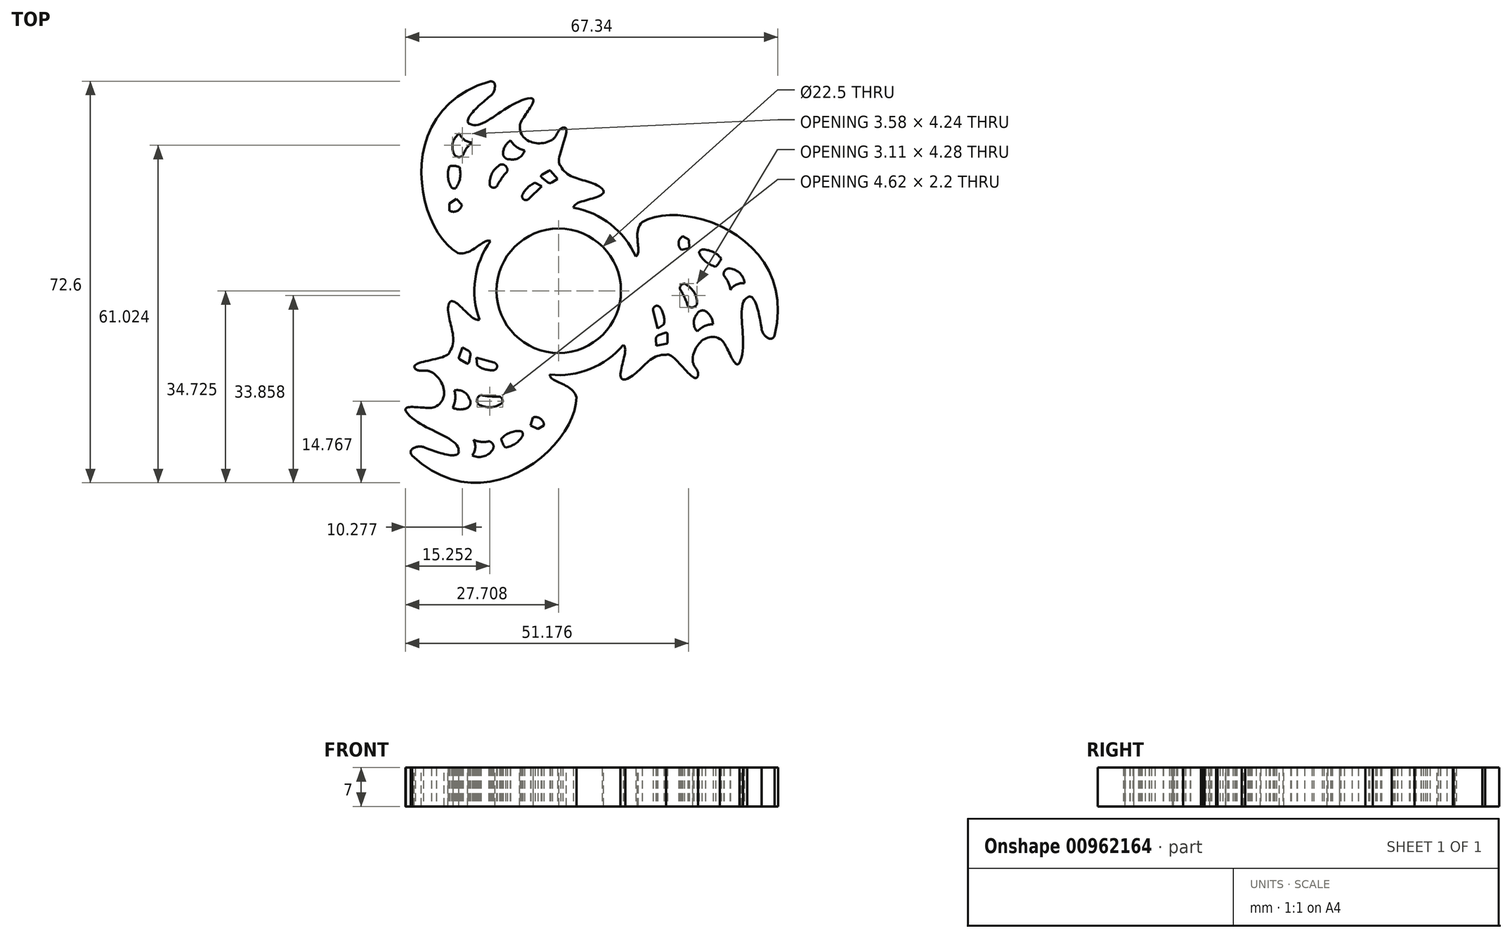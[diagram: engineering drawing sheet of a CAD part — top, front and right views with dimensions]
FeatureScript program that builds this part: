
annotation { "Feature Type Name" : "Feature", "Feature Type Description" : "" }
export const myFeature = defineFeature(function(context is Context, id is Id, definition is map)
    precondition{}
    {
        {
            var Q0;
            Q0=qCreatedBy(makeId("Top.planeOp"),FACE);
            var sketch = newSketch(context, id + "F0", { "sketchPlane" : qUnion([Q0])});
            skCircle(sketch, "E0", {"center": v(0.74, -90.82) * mm, "radius": 11.25 * mm});
            skCircle(sketch, "E1.0", {"center": v(0.74, -90.82) * mm, "radius": 15.25 * mm});
            skFitSpline(sketch, "E2", {"points": [v(-11.6, -81.84) * mm, v(-17.53, -83.96) * mm], "startDerivative": vector(-4, 2.16) * mm, "endDerivative": vector(-7.86, 2) * mm});
            skFitSpline(sketch, "E3", {"points": [v(-17.53, -83.96) * mm, v(-11.8, -52.97) * mm], "startDerivative": vector(-23.07, 13.08) * mm, "endDerivative": vector(52.2, 15.17) * mm});
            skFitSpline(sketch, "E4", {"points": [v(-11.8, -52.97) * mm, v(-11.47, -55.48) * mm], "startDerivative": vector(4.5, 0.84) * mm, "endDerivative": vector(-2.3, -1.99) * mm});
            skFitSpline(sketch, "E5", {"points": [v(-11.47, -55.48) * mm, v(-15.25, -60.7) * mm], "startDerivative": vector(-5.39, -4.17) * mm, "endDerivative": vector(5.26, -2.02) * mm});
            skFitSpline(sketch, "E6", {"points": [v(-15.25, -60.7) * mm, v(-4.3, -55.98) * mm], "startDerivative": vector(7.24, -3.74) * mm, "endDerivative": vector(12.54, 1.2) * mm});
            skFitSpline(sketch, "E7", {"points": [v(-4.3, -55.98) * mm, v(-6.3, -61.23) * mm], "startDerivative": vector(5.26, -0.77) * mm, "endDerivative": vector(0.49, -4.52) * mm});
            skFitSpline(sketch, "E8", {"points": [v(-6.3, -61.23) * mm, v(-0.45, -63.53) * mm], "startDerivative": vector(0.14, -8.53) * mm, "endDerivative": vector(6.56, 4) * mm});
            skFitSpline(sketch, "E9", {"points": [v(-0.45, -63.53) * mm, v(1.48, -61.32) * mm], "startDerivative": vector(2.9, 1.83) * mm, "endDerivative": vector(3, 0.9) * mm});
            skFitSpline(sketch, "E10", {"points": [v(1.48, -61.32) * mm, v(1.08, -68.23) * mm], "startDerivative": vector(6.34, 1.41) * mm, "endDerivative": vector(4.15, -2.92) * mm});
            skFitSpline(sketch, "E11", {"points": [v(1.08, -68.23) * mm, v(8.6, -72.36) * mm], "startDerivative": vector(4.35, -8.75) * mm, "endDerivative": vector(6.74, -5.79) * mm});
            skFitSpline(sketch, "E12", {"points": [v(8.6, -72.36) * mm, v(3.4, -75.8) * mm], "startDerivative": vector(4.7, -5.65) * mm, "endDerivative": vector(-0.3, -4.9) * mm});
            skArc(sketch, "E13", {"start": v(-17.21, -62.4) * mm, "mid": v(-16.3, -63.55) * mm, "end": v(-14.9, -64.02) * mm});
            skArc(sketch, "E14", {"start": v(-17.21, -62.4) * mm, "mid": v(-18.38, -64) * mm, "end": v(-18.23, -65.98) * mm});
            skArc(sketch, "E15", {"start": v(-18.23, -65.98) * mm, "mid": v(-17.47, -66.62) * mm, "end": v(-16.53, -66.27) * mm});
            skArc(sketch, "E16", {"start": v(-14.9, -64.02) * mm, "mid": v(-15.9, -65.01) * mm, "end": v(-16.53, -66.27) * mm});
            skArc(sketch, "E17", {"start": v(-17.9, -72.28) * mm, "mid": v(-17.1, -70.45) * mm, "end": v(-17.21, -68.45) * mm});
            skArc(sketch, "E18", {"start": v(-19, -68.3) * mm, "mid": v(-19.28, -70.25) * mm, "end": v(-18.65, -72.11) * mm});
            skArc(sketch, "E19", {"start": v(-18.65, -72.11) * mm, "mid": v(-18.3, -72.31) * mm, "end": v(-17.9, -72.28) * mm});
            skArc(sketch, "E20", {"start": v(-17.21, -68.45) * mm, "mid": v(-18.1, -68.24) * mm, "end": v(-19, -68.3) * mm});
            skArc(sketch, "E21", {"start": v(-9.73, -67.97) * mm, "mid": v(-11.32, -69.58) * mm, "end": v(-11.7, -71.8) * mm});
            skArc(sketch, "E22", {"start": v(-11.7, -71.8) * mm, "mid": v(-11.13, -72.18) * mm, "end": v(-10.48, -71.97) * mm});
            skArc(sketch, "E23", {"start": v(-8.56, -69.2) * mm, "mid": v(-9.6, -70.53) * mm, "end": v(-10.48, -71.97) * mm});
            skArc(sketch, "E24", {"start": v(-8.56, -69.2) * mm, "mid": v(-8.83, -68.29) * mm, "end": v(-9.73, -67.97) * mm});
            skArc(sketch, "E25", {"start": v(-7.98, -63.64) * mm, "mid": v(-8.94, -64.65) * mm, "end": v(-9.35, -65.98) * mm});
            skArc(sketch, "E26", {"start": v(-9.35, -65.98) * mm, "mid": v(-8.94, -66.8) * mm, "end": v(-8.05, -67.05) * mm});
            skArc(sketch, "E27", {"start": v(-8.05, -67.05) * mm, "mid": v(-6.43, -66.76) * mm, "end": v(-5.43, -65.46) * mm});
            skArc(sketch, "E28", {"start": v(-7.98, -63.64) * mm, "mid": v(-6.88, -64.8) * mm, "end": v(-5.43, -65.46) * mm});
            skArc(sketch, "E29", {"start": v(-19, -76.35) * mm, "mid": v(-17.63, -76.39) * mm, "end": v(-16.77, -75.31) * mm});
            skLineSegment(sketch, "E30", {"start": v(-19, -76.35) * mm, "end": v(-19, -75.05) * mm});
            skLineSegment(sketch, "E31", {"start": v(-19, -75.05) * mm, "end": v(-17.77, -74.22) * mm});
            skLineSegment(sketch, "E32", {"start": v(-17.77, -74.22) * mm, "end": v(-16.77, -75.31) * mm});
            skLineSegment(sketch, "E33", {"start": v(-3.53, -71.3) * mm, "end": v(-2.3, -71.91) * mm});
            skLineSegment(sketch, "E34", {"start": v(-2.3, -71.91) * mm, "end": v(-4.7, -74.23) * mm});
            skArc(sketch, "E35", {"start": v(-5.8, -73.43) * mm, "mid": v(-5.6, -74.3) * mm, "end": v(-4.7, -74.23) * mm});
            skArc(sketch, "E36", {"start": v(-3.53, -71.3) * mm, "mid": v(-4.87, -72.15) * mm, "end": v(-5.8, -73.43) * mm});
            skArc(sketch, "E37", {"start": v(-2.3, -69.83) * mm, "mid": v(-2.44, -70.06) * mm, "end": v(-2.34, -70.32) * mm});
            skLineSegment(sketch, "E38", {"start": v(-2.3, -69.83) * mm, "end": v(-1.05, -69.13) * mm});
            skArc(sketch, "E39", {"start": v(-0.73, -69.13) * mm, "mid": v(-0.9, -69.09) * mm, "end": v(-1.05, -69.13) * mm});
            skLineSegment(sketch, "E40", {"start": v(-0.73, -69.13) * mm, "end": v(0.54, -70.6) * mm});
            skLineSegment(sketch, "E41", {"start": v(0.54, -70.6) * mm, "end": v(-0.47, -71.23) * mm});
            skArc(sketch, "E42", {"start": v(-1.3, -71.18) * mm, "mid": v(-0.9, -71.34) * mm, "end": v(-0.47, -71.23) * mm});
            skLineSegment(sketch, "E43", {"start": v(-1.3, -71.18) * mm, "end": v(-2.34, -70.32) * mm});
            skLineSegment(sketch, "E44", {"start": v(-11.6, -81.84) * mm, "end": v(-10.71, -82.21) * mm});
            skLineSegment(sketch, "E45", {"start": v(3.4, -75.8) * mm, "end": v(3.39, -75.8) * mm});
            skArc(sketch, "E46.1.0", {"start": v(-13.81, -111.3) * mm, "mid": v(-11.62, -111.87) * mm, "end": v(-9.5, -111.1) * mm});
            skArc(sketch, "E46.1.1", {"start": v(-14.64, -117.76) * mm, "mid": v(-13.29, -118.13) * mm, "end": v(-11.89, -118.04) * mm});
            skArc(sketch, "E46.1.2", {"start": v(-9.65, -117.54) * mm, "mid": v(-9.4, -118.42) * mm, "end": v(-8.88, -119.17) * mm});
            skArc(sketch, "E46.1.3", {"start": v(-14.9, -120.57) * mm, "mid": v(-12.92, -120.78) * mm, "end": v(-11.29, -119.67) * mm});
            skArc(sketch, "E46.1.4", {"start": v(-6, -116.22) * mm, "mid": v(-7.98, -116.44) * mm, "end": v(-9.65, -117.54) * mm});
            skArc(sketch, "E46.1.5", {"start": v(-1.92, -115.15) * mm, "mid": v(-2.57, -113.94) * mm, "end": v(-3.93, -113.73) * mm});
            skArc(sketch, "E46.1.6", {"start": v(-13.33, -109.67) * mm, "mid": v(-11.66, -109.91) * mm, "end": v(-9.97, -109.96) * mm});
            skArc(sketch, "E46.1.7", {"start": v(-18.44, -111.95) * mm, "mid": v(-17.09, -112.28) * mm, "end": v(-15.73, -111.97) * mm});
            skArc(sketch, "E46.1.8", {"start": v(-18.44, -111.95) * mm, "mid": v(-17.98, -110.42) * mm, "end": v(-18.14, -108.83) * mm});
            skArc(sketch, "E46.1.9", {"start": v(-15.73, -111.97) * mm, "mid": v(-15.22, -111.2) * mm, "end": v(-15.45, -110.3) * mm});
            skArc(sketch, "E46.1.10", {"start": v(-15.45, -110.3) * mm, "mid": v(-16.5, -109.05) * mm, "end": v(-18.14, -108.83) * mm});
            skArc(sketch, "E46.1.11", {"start": v(-14.9, -120.57) * mm, "mid": v(-14.36, -119.2) * mm, "end": v(-14.64, -117.76) * mm});
            skArc(sketch, "E46.1.12", {"start": v(-13.33, -109.67) * mm, "mid": v(-13.99, -110.37) * mm, "end": v(-13.81, -111.3) * mm});
            skArc(sketch, "E46.1.13", {"start": v(-11.29, -119.67) * mm, "mid": v(-11.1, -118.68) * mm, "end": v(-11.89, -118.04) * mm});
            skArc(sketch, "E46.1.14", {"start": v(-9.5, -111.1) * mm, "mid": v(-9.47, -110.42) * mm, "end": v(-9.97, -109.96) * mm});
            skArc(sketch, "E46.1.15", {"start": v(-5.76, -116.96) * mm, "mid": v(-5.77, -116.56) * mm, "end": v(-6, -116.22) * mm});
            skArc(sketch, "E46.1.16", {"start": v(-8.88, -119.17) * mm, "mid": v(-7.06, -118.43) * mm, "end": v(-5.76, -116.96) * mm});
            skLineSegment(sketch, "E46.1.17", {"start": v(-4.38, -115.14) * mm, "end": v(-3.93, -113.73) * mm});
            skLineSegment(sketch, "E46.1.18", {"start": v(-14.11, -102.9) * mm, "end": v(-10.9, -103.82) * mm});
            skLineSegment(sketch, "E46.1.19", {"start": v(-1.92, -115.15) * mm, "end": v(-3.04, -115.8) * mm});
            skLineSegment(sketch, "E46.1.20", {"start": v(-0.87, -105.98) * mm, "end": v(-0.99, -105.03) * mm});
            skArc(sketch, "E46.1.21", {"start": v(-14.03, -104.27) * mm, "mid": v(-12.62, -105) * mm, "end": v(-11.05, -105.18) * mm});
            skArc(sketch, "E46.1.22", {"start": v(-11.05, -105.18) * mm, "mid": v(-10.4, -104.56) * mm, "end": v(-10.9, -103.82) * mm});
            skLineSegment(sketch, "E46.1.23", {"start": v(-3.04, -115.8) * mm, "end": v(-4.38, -115.14) * mm});
            skLineSegment(sketch, "E46.1.24", {"start": v(-17.3, -102.93) * mm, "end": v(-16.67, -101.1) * mm});
            skLineSegment(sketch, "E46.1.25", {"start": v(-13.6, -96.02) * mm, "end": v(-13.59, -96.02) * mm});
            skArc(sketch, "E46.1.26", {"start": v(-17.3, -102.93) * mm, "mid": v(-17.26, -103.1) * mm, "end": v(-17.15, -103.2) * mm});
            skArc(sketch, "E46.1.27", {"start": v(-15.25, -102.4) * mm, "mid": v(-15.31, -101.97) * mm, "end": v(-15.62, -101.66) * mm});
            skArc(sketch, "E46.1.28", {"start": v(-15.92, -103.93) * mm, "mid": v(-15.64, -103.94) * mm, "end": v(-15.48, -103.73) * mm});
            skLineSegment(sketch, "E46.1.29", {"start": v(-14.03, -104.27) * mm, "end": v(-14.11, -102.9) * mm});
            skLineSegment(sketch, "E46.1.30", {"start": v(-15.25, -102.4) * mm, "end": v(-15.48, -103.73) * mm});
            skLineSegment(sketch, "E46.1.31", {"start": v(-15.92, -103.93) * mm, "end": v(-17.15, -103.2) * mm});
            skLineSegment(sketch, "E46.1.32", {"start": v(-16.67, -101.1) * mm, "end": v(-15.62, -101.66) * mm});
            skArc(sketch, "E46.2.0", {"start": v(25.76, -93.17) * mm, "mid": v(25.16, -91) * mm, "end": v(23.42, -89.54) * mm});
            skArc(sketch, "E46.2.1", {"start": v(31.76, -90.67) * mm, "mid": v(31.4, -89.3) * mm, "end": v(30.63, -88.14) * mm});
            skArc(sketch, "E46.2.2", {"start": v(29.08, -86.45) * mm, "mid": v(29.7, -85.79) * mm, "end": v(30.1, -84.97) * mm});
            skArc(sketch, "E46.2.3", {"start": v(34.33, -89.48) * mm, "mid": v(33.52, -87.67) * mm, "end": v(31.74, -86.8) * mm});
            skArc(sketch, "E46.2.4", {"start": v(26.1, -83.94) * mm, "mid": v(27.3, -85.55) * mm, "end": v(29.08, -86.45) * mm});
            skArc(sketch, "E46.2.5", {"start": v(23.14, -80.95) * mm, "mid": v(22.42, -82.12) * mm, "end": v(22.92, -83.4) * mm});
            skArc(sketch, "E46.2.6", {"start": v(24.1, -93.57) * mm, "mid": v(23.48, -92) * mm, "end": v(22.67, -90.52) * mm});
            skArc(sketch, "E46.2.7", {"start": v(28.63, -96.85) * mm, "mid": v(28.24, -95.52) * mm, "end": v(27.3, -94.5) * mm});
            skArc(sketch, "E46.2.8", {"start": v(28.63, -96.85) * mm, "mid": v(27.08, -97.22) * mm, "end": v(25.78, -98.16) * mm});
            skArc(sketch, "E46.2.9", {"start": v(27.3, -94.5) * mm, "mid": v(26.37, -94.44) * mm, "end": v(25.71, -95.09) * mm});
            skArc(sketch, "E46.2.10", {"start": v(25.71, -95.09) * mm, "mid": v(25.15, -96.63) * mm, "end": v(25.78, -98.16) * mm});
            skArc(sketch, "E46.2.11", {"start": v(34.33, -89.48) * mm, "mid": v(32.87, -89.7) * mm, "end": v(31.76, -90.67) * mm});
            skArc(sketch, "E46.2.12", {"start": v(24.1, -93.57) * mm, "mid": v(25.03, -93.8) * mm, "end": v(25.76, -93.17) * mm});
            skArc(sketch, "E46.2.13", {"start": v(31.74, -86.8) * mm, "mid": v(30.8, -87.14) * mm, "end": v(30.63, -88.14) * mm});
            skArc(sketch, "E46.2.14", {"start": v(23.42, -89.54) * mm, "mid": v(22.82, -89.85) * mm, "end": v(22.67, -90.52) * mm});
            skArc(sketch, "E46.2.15", {"start": v(26.63, -83.37) * mm, "mid": v(26.28, -83.58) * mm, "end": v(26.1, -83.94) * mm});
            skArc(sketch, "E46.2.16", {"start": v(30.1, -84.97) * mm, "mid": v(28.55, -83.76) * mm, "end": v(26.63, -83.37) * mm});
            skLineSegment(sketch, "E46.2.17", {"start": v(24.36, -83.08) * mm, "end": v(22.92, -83.4) * mm});
            skLineSegment(sketch, "E46.2.18", {"start": v(18.63, -97.63) * mm, "end": v(17.82, -94.4) * mm});
            skLineSegment(sketch, "E46.2.19", {"start": v(23.14, -80.95) * mm, "end": v(24.26, -81.6) * mm});
            skLineSegment(sketch, "E46.2.20", {"start": v(14.68, -84.62) * mm, "end": v(13.91, -85.2) * mm});
            skArc(sketch, "E46.2.21", {"start": v(19.78, -96.88) * mm, "mid": v(19.7, -95.3) * mm, "end": v(19.07, -93.84) * mm});
            skArc(sketch, "E46.2.22", {"start": v(19.07, -93.84) * mm, "mid": v(18.21, -93.6) * mm, "end": v(17.82, -94.4) * mm});
            skLineSegment(sketch, "E46.2.23", {"start": v(24.26, -81.6) * mm, "end": v(24.36, -83.08) * mm});
            skLineSegment(sketch, "E46.2.24", {"start": v(20.26, -100.39) * mm, "end": v(18.35, -100.75) * mm});
            skLineSegment(sketch, "E46.2.25", {"start": v(12.42, -100.62) * mm, "end": v(12.41, -100.62) * mm});
            skArc(sketch, "E46.2.26", {"start": v(20.26, -100.39) * mm, "mid": v(20.37, -100.27) * mm, "end": v(20.42, -100.1) * mm});
            skArc(sketch, "E46.2.27", {"start": v(18.77, -98.87) * mm, "mid": v(18.42, -99.14) * mm, "end": v(18.3, -99.56) * mm});
            skArc(sketch, "E46.2.28", {"start": v(20.43, -98.68) * mm, "mid": v(20.3, -98.44) * mm, "end": v(20.03, -98.4) * mm});
            skLineSegment(sketch, "E46.2.29", {"start": v(19.78, -96.88) * mm, "end": v(18.63, -97.63) * mm});
            skLineSegment(sketch, "E46.2.30", {"start": v(18.77, -98.87) * mm, "end": v(20.03, -98.4) * mm});
            skLineSegment(sketch, "E46.2.31", {"start": v(20.43, -98.68) * mm, "end": v(20.42, -100.1) * mm});
            skLineSegment(sketch, "E46.2.32", {"start": v(18.35, -100.75) * mm, "end": v(18.3, -99.56) * mm});
            skArc(sketch, "E47", {"start": v(3.4, -75.8) * mm, "mid": v(-4.93, -76.75) * mm, "end": v(-11.6, -81.84) * mm});
            skSolve(sketch);
        }
        {
            var Q0;
            {var subQ1=sQuery(id+"F0.wireOp",EDGE,"E2");Q0=makeQuery(id+"F0.imprint","IMPRINT",FACE,{"disambiguationData":[TD([[makeQuery(id+"F0.imprint","IMPRINT",EDGE,{"derivedFrom":subQ1}),-1.0]])]});}
            var Q1;
            Q1=makeQuery(id+"F0.imprint","IMPRINT",FACE,{"disambiguationData":[TD([[makeQuery(id+"F0.imprint","IMPRINT",EDGE,{"derivedFrom":sQuery(id+"F0.wireOp",EDGE,"E0")}),-1.0]])]});
            var Q2;
            {var subQ0=sQuery(id+"F0.wireOp",EDGE,"E47");Q2=makeQuery(id+"F0.imprint","IMPRINT",FACE,{"disambiguationData":[TD([[makeQuery(id+"F0.imprint","IMPRINT",EDGE,{"derivedFrom":subQ0}),-1.0]])]});}
            extrude(context, id + "F1", {"entities" : qUnion([Q0, Q1, Q2]), "depth" : 7 * mm, "offsetDistance" : 25 * mm});
        }
        {
            var Q0;
            Q0=makeQuery(id+"F1.opExtrude","SWEPT_BODY",BODY,{"disambiguationData":[OSD([sQuery(id+"F0.wireOp",EDGE,"E0"),sQuery(id+"F0.wireOp",EDGE,"E1.0"),sQuery(id+"F0.wireOp",EDGE,"E2"),sQuery(id+"F0.wireOp",EDGE,"E3"),sQuery(id+"F0.wireOp",EDGE,"E4"),sQuery(id+"F0.wireOp",EDGE,"E5"),sQuery(id+"F0.wireOp",EDGE,"E6"),sQuery(id+"F0.wireOp",EDGE,"E7"),sQuery(id+"F0.wireOp",EDGE,"E8"),sQuery(id+"F0.wireOp",EDGE,"E9"),sQuery(id+"F0.wireOp",EDGE,"E10"),sQuery(id+"F0.wireOp",EDGE,"E11"),sQuery(id+"F0.wireOp",EDGE,"E12"),sQuery(id+"F0.wireOp",EDGE,"E13"),sQuery(id+"F0.wireOp",EDGE,"E14"),sQuery(id+"F0.wireOp",EDGE,"E15"),sQuery(id+"F0.wireOp",EDGE,"E16"),sQuery(id+"F0.wireOp",EDGE,"E17"),sQuery(id+"F0.wireOp",EDGE,"E18"),sQuery(id+"F0.wireOp",EDGE,"E19"),sQuery(id+"F0.wireOp",EDGE,"E20"),sQuery(id+"F0.wireOp",EDGE,"E21"),sQuery(id+"F0.wireOp",EDGE,"E22"),sQuery(id+"F0.wireOp",EDGE,"E23"),sQuery(id+"F0.wireOp",EDGE,"E24"),sQuery(id+"F0.wireOp",EDGE,"E25"),sQuery(id+"F0.wireOp",EDGE,"E26"),sQuery(id+"F0.wireOp",EDGE,"E27"),sQuery(id+"F0.wireOp",EDGE,"E28"),sQuery(id+"F0.wireOp",EDGE,"E29"),sQuery(id+"F0.wireOp",EDGE,"E30"),sQuery(id+"F0.wireOp",EDGE,"E31"),sQuery(id+"F0.wireOp",EDGE,"E32"),sQuery(id+"F0.wireOp",EDGE,"E33"),sQuery(id+"F0.wireOp",EDGE,"E34"),sQuery(id+"F0.wireOp",EDGE,"E35"),sQuery(id+"F0.wireOp",EDGE,"E36"),sQuery(id+"F0.wireOp",EDGE,"E37"),sQuery(id+"F0.wireOp",EDGE,"E38"),sQuery(id+"F0.wireOp",EDGE,"E39"),sQuery(id+"F0.wireOp",EDGE,"E40"),sQuery(id+"F0.wireOp",EDGE,"E41"),sQuery(id+"F0.wireOp",EDGE,"E42"),sQuery(id+"F0.wireOp",EDGE,"E43")])]});
            var Q1;
            Q1=makeQuery(id+"F1.opExtrude","CAP_EDGE",EDGE,{"disambiguationData":[OSD([sQuery(id+"F0.wireOp",EDGE,"E0")])],"isStart":false});
            circularPattern(context, id + "F2", {"operationType" : NewBodyOperationType.ADD, "entities" : qUnion([Q0]), "axis" : qUnion([Q1]), "angle" : 360 * degree, "instanceCount" : 3, "equalSpace" : true});
        }
    });
